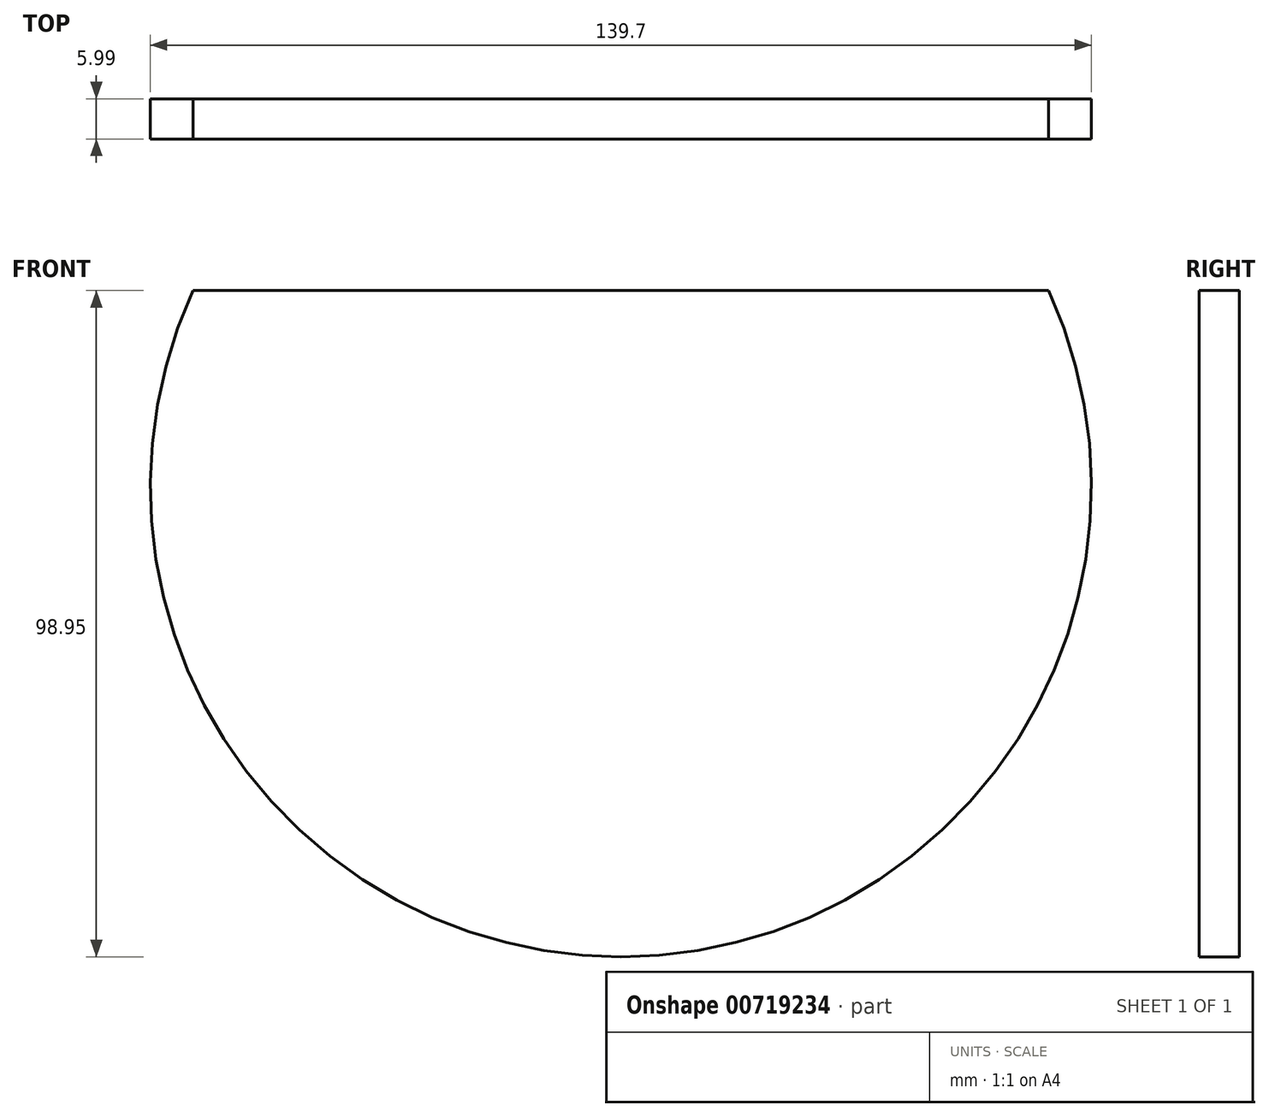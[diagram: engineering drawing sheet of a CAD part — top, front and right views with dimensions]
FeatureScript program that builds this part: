
annotation { "Feature Type Name" : "Feature", "Feature Type Description" : "" }
export const myFeature = defineFeature(function(context is Context, id is Id, definition is map)
    precondition{}
    {
        {
            var Q0;
            Q0=qCreatedBy(makeId("Front.planeOp"),FACE);
            var sketch = newSketch(context, id + "F0", { "sketchPlane" : qUnion([Q0])});
            skArc(sketch, "E0", {"start": v(-63.5, 29.1) * mm, "mid": v(0, -69.85) * mm, "end": v(63.5, 29.1) * mm});
            skLineSegment(sketch, "E1", {"start": v(0, 0) * mm, "end": v(0, 29.1) * mm, "construction": true});
            skLineSegment(sketch, "E2", {"start": v(-63.5, 29.1) * mm, "end": v(-15.24, 29.1) * mm});
            skLineSegment(sketch, "E3", {"start": v(63.5, 29.1) * mm, "end": v(15.24, 29.1) * mm});
            skLineSegment(sketch, "E4", {"start": v(-15.24, 29.1) * mm, "end": v(15.24, 29.1) * mm});
            skSolve(sketch);
        }
        {
            var Q0;
            Q0=makeQuery(id+"F0.imprint","IMPRINT",FACE,{"disambiguationData":[TD([[makeQuery(id+"F0.imprint","IMPRINT",EDGE,{"derivedFrom":sQuery(id+"F0.wireOp",EDGE,"E0")}),1.0]])]});
            extrude(context, id + "F1", {"entities" : qUnion([Q0]), "depth" : 6 * mm, "offsetDistance" : 25.4 * mm});
        }
    });
